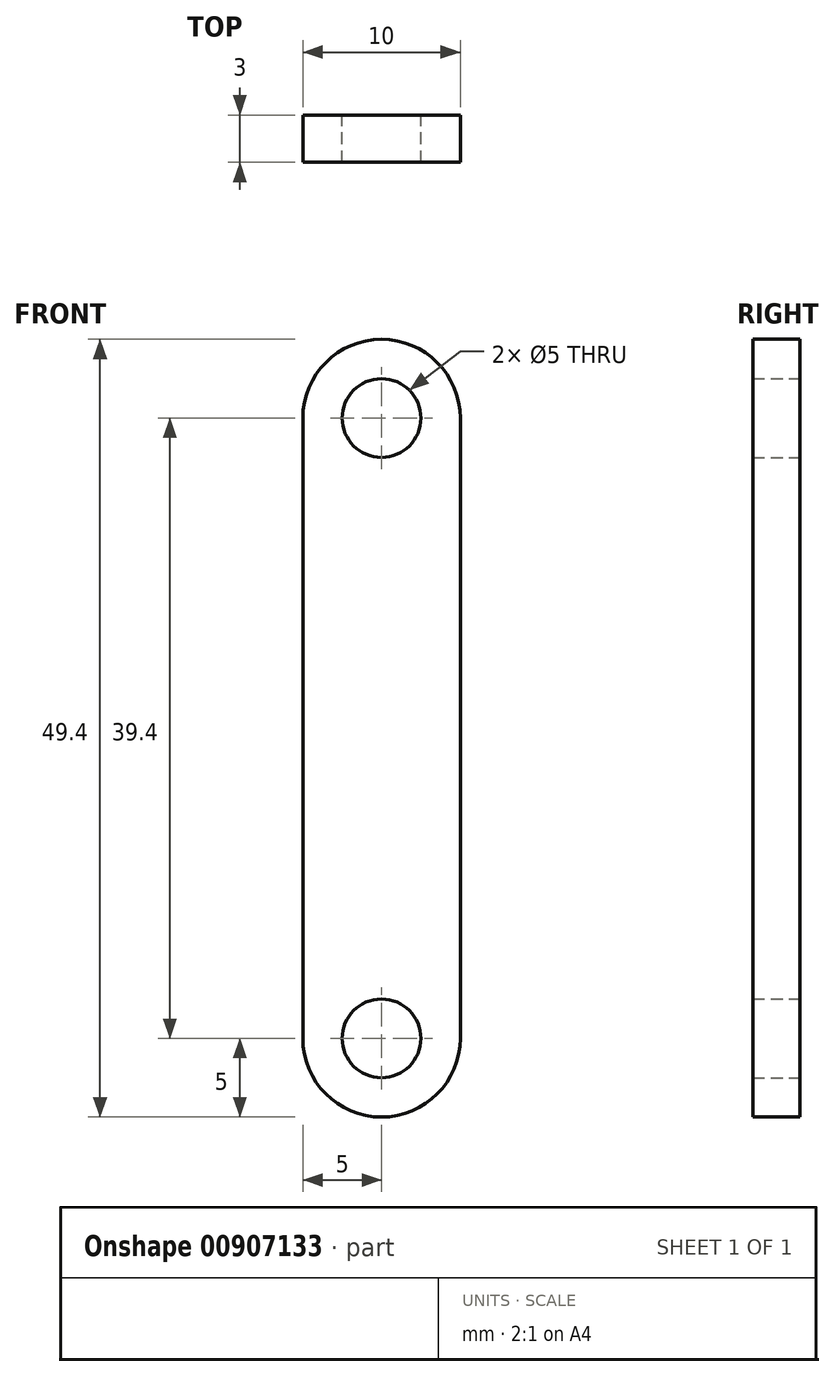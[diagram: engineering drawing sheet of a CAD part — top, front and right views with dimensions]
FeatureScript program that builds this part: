
annotation { "Feature Type Name" : "Feature", "Feature Type Description" : "" }
export const myFeature = defineFeature(function(context is Context, id is Id, definition is map)
    precondition{}
    {
        {
            var Q0;
            Q0=qCreatedBy(makeId("Front.planeOp"),FACE);
            var sketch = newSketch(context, id + "F0", { "sketchPlane" : qUnion([Q0])});
            skLineSegment(sketch, "E0.left", {"start": v(5, 19.7) * mm, "end": v(5, -19.7) * mm});
            skLineSegment(sketch, "E0.right", {"start": v(-5, 19.7) * mm, "end": v(-5, -19.7) * mm});
            skPoint(sketch, "E0.middle", {"position": v(0, 0) * mm});
            skArc(sketch, "E1", {"start": v(5, 19.7) * mm, "mid": v(0, 24.7) * mm, "end": v(-5, 19.7) * mm});
            skArc(sketch, "E2", {"start": v(-5, -19.7) * mm, "mid": v(0, -24.7) * mm, "end": v(5, -19.7) * mm});
            skCircle(sketch, "E3", {"center": v(0, 19.7) * mm, "radius": 2.5 * mm});
            skCircle(sketch, "E4", {"center": v(0, -19.7) * mm, "radius": 2.5 * mm});
            skSolve(sketch);
        }
        {
            var Q0;
            Q0=qSketchRegion(id+"F0",true);
            extrude(context, id + "F1", {"entities" : qUnion([Q0]), "depth" : 3 * mm, "offsetDistance" : 25 * mm});
        }
    });
